# Revit family: KEUCO_14909011037_
name_source: partatom
category: Generic Models
revit_build: Autodesk Revit 2016 (Build: 20150220_1215(x64)
units: mm (PartAtom-declared; Revit-internal decimal feet)

## family parameters
Always vertical = No
Can host rebar = No
Cut with Voids When Loaded = No
Part Type = Normal
Room Calculation Point = No
Round Connector Dimension = Use Diameter
Shared = No
Work Plane-Based = Yes

## types (9) — shared parameters
Default Elevation = 1219 mm
Manufacturer = KEUCO
Serie = Plan
URL = https://www.keuco.com
zero-valued in all types: Gewicht

## per-type parameters (varying)
| type | Ausschreibungstext | Description | Material Tablett | Rahmen Material |
| 14909011037 | KEUCO PLAN Winkelgriff 135° mit Seifenablage, rechte Ausführung, 14909011037
hochglanzverchromter Winkelgriff 135° mit integrierter Seifenablage, 
in ästhetischem, funktionalem Design
rechte Ausführung,
speziell für Wannen-Bereich, als Hilfe zum Festhalten und Abstützen, 
mit integrierter Seifenablage aus Kunststoff (schlagzähes Polysterol), schwarzgrau (RAL 7021),
Ablagefläche 154 mm Breite, 23 mm Höhe, Tiefe 67 mm,
Winkelgriff bis 115 kg belastbar, antistatisch, leicht zu reinigen,
Außenmaß gesamt 444/201 mm,
Rohrdurchmesser 25 mm, 3 Befestigungspunkte, 
Gesamtbreite 444 mm, Gesamthöhe 201 mm, 
Ausladung 108 mm, Wandabstand 83 mm
Der Winkelgriff wird verdeckt angebracht

Lieferung inkl. korrosionsfreiem Befestigungsmaterial | mit Seifenablage, rechte Ausführung | Lichtgrau (RAL 7035) | Edelstahl |
| 14909011038 | KEUCO PLAN Winkelgriff 135° mit Seifenablage, rechte Ausführung, 14909011038
hochglanzverchromter Winkelgriff 135° mit integrierter Seifenablage, 
in ästhetischem, funktionalem Design
rechte Ausführung,
speziell für Wannen-Bereich, als Hilfe zum Festhalten und Abstützen, 
mit integrierter Seifenablage aus Kunststoff (schlagzähes Polysterol), lichtgrau (RAL 7035),
Ablagefläche 154 mm Breite, 23 mm Höhe, Tiefe 67 mm,
Winkelgriff bis 115 kg belastbar, antistatisch, leicht zu reinigen,
Außenmaß gesamt 444/201 mm,
Rohrdurchmesser 25 mm, 3 Befestigungspunkte, 
Gesamtbreite 444 mm, Gesamthöhe 201 mm, 
Ausladung 108 mm, Wandabstand 83 mm
Der Winkelgriff wird verdeckt angebracht

Lieferung inkl. korrosionsfreiem Befestigungsmaterial | mit Seifenablage, rechte Ausführung | Lichtgrau (RAL 7035) | verchromt |
| 14909011051 | KEUCO PLAN Winkelgriff 135° mit Seifenablage, rechte Ausführung, 14909011051
hochglanzverchromter Winkelgriff 135° mit integrierter Seifenablage, 
in ästhetischem, funktionalem Design
rechte Ausführung,
speziell für Wannen-Bereich, als Hilfe zum Festhalten und Abstützen, 
mit integrierter Seifenablage aus Kunststoff (schlagzähes Polysterol), weiß (RAL 9010),
Ablagefläche 154 mm Breite, 23 mm Höhe, Tiefe 67 mm,
Winkelgriff bis 115 kg belastbar, antistatisch, leicht zu reinigen,
Außenmaß gesamt 444/201 mm,
Rohrdurchmesser 25 mm, 3 Befestigungspunkte, 
Gesamtbreite 444 mm, Gesamthöhe 201 mm, 
Ausladung 108 mm, Wandabstand 83 mm
Der Winkelgriff wird verdeckt angebracht

Lieferung inkl. korrosionsfreiem Befestigungsmaterial | mit Seifenablage, rechte Ausführung | Weiß (RAL 9010) | verchromt |
| 14909071037 | KEUCO PLAN Winkelgriff 135° mit Seifenablage, rechte Ausführung, 14909071037
Winkelgriff 135° aus hochwertigem Edelstahl mit integrierter Seifenablage, 
in ästhetischem, funktionalem Design
rechte Ausführung,
speziell für Wannen-Bereich, als Hilfe zum Festhalten und Abstützen, 
mit integrierter Seifenablage aus Kunststoff (schlagzähes Polysterol), schwarzgrau (RAL 7021),
Ablagefläche 154 mm Breite, 23 mm Höhe, Tiefe 67 mm,
Winkelgriff bis 115 kg belastbar, antistatisch, leicht zu reinigen,
Außenmaß gesamt 444/201 mm,
Rohrdurchmesser 25 mm, 3 Befestigungspunkte, 
Gesamtbreite 444 mm, Gesamthöhe 201 mm, 
Ausladung 108 mm, Wandabstand 83 mm
Der Winkelgriff wird verdeckt angebracht

Lieferung inkl. korrosionsfreiem Befestigungsmaterial | mit Seifenablage, rechte Ausführung | schwarzgrau (RAL 7021) | Edelstahl |
| 14909071038 | KEUCO PLAN Winkelgriff 135° mit Seifenablage, rechte Ausführung, 14909071038
Winkelgriff 135° aus hochwertigem Edelstahl mit integrierter Seifenablage, 
in ästhetischem, funktionalem Design
rechte Ausführung,
speziell für Wannen-Bereich, als Hilfe zum Festhalten und Abstützen, 
mit integrierter Seifenablage aus Kunststoff (schlagzähes Polysterol), .lichtgrau (RAL 7035,
Ablagefläche 154 mm Breite, 23 mm Höhe, Tiefe 67 mm,
Winkelgriff bis 115 kg belastbar, antistatisch, leicht zu reinigen,
Außenmaß gesamt 444/201 mm,
Rohrdurchmesser 25 mm, 3 Befestigungspunkte, 
Gesamtbreite 444 mm, Gesamthöhe 201 mm, 
Ausladung 108 mm, Wandabstand 83 mm
Der Winkelgriff wird verdeckt angebracht

Lieferung inkl. korrosionsfreiem Befestigungsmaterial | mit Seifenablage, rechte Ausführung | Lichtgrau (RAL 7035) | Edelstahl |
| 14909071051 | KEUCO PLAN Winkelgriff 135° mit Seifenablage, rechte Ausführung, 14909071051
Winkelgriff 135° aus hochwertigem Edelstahl mit integrierter Seifenablage, 
in ästhetischem, funktionalem Design
rechte Ausführung,
speziell für Wannen-Bereich, als Hilfe zum Festhalten und Abstützen, 
mit integrierter Seifenablage aus Kunststoff (schlagzähes Polysterol), weiß (RAL 9010
Ablagefläche 154 mm Breite, 23 mm Höhe, Tiefe 67 mm,
Winkelgriff bis 115 kg belastbar, antistatisch, leicht zu reinigen,
Außenmaß gesamt 444/201 mm,
Rohrdurchmesser 25 mm, 3 Befestigungspunkte, 
Gesamtbreite 444 mm, Gesamthöhe 201 mm, 
Ausladung 108 mm, Wandabstand 83 mm
Der Winkelgriff wird verdeckt angebracht

Lieferung inkl. korrosionsfreiem Befestigungsmaterial | mit Seifenablage, rechte Ausführung | Weiß (RAL 9010) | Edelstahl |
| 14909171037 |  | -- | schwarzgrau (RAL 7021) | Aluminium silber-eloxiert (E6 EV1)Aluminium 1100-H18 |
| 14909171038 | KEUCO PLAN Winkelgriff 135° mit Seifenablage, rechte Ausführung, 14909171038
Winkelgriff 135° aus silber-eloxiertem Aluminium mit integrierter Seifenablage, 
in ästhetischem, funktionalem Design
rechte Ausführung,
speziell für Wannen-Bereich, als Hilfe zum Festhalten und Abstützen, 
mit integrierter Seifenablage aus Kunststoff (schlagzähes Polysterol), lichtgrau (RAL 7035),
Ablagefläche 154 mm Breite, 23 mm Höhe, Tiefe 67 mm,
Winkelgriff bis 115 kg belastbar, antistatisch, leicht zu reinigen,
Außenmaß gesamt 444/201 mm,
Rohrdurchmesser 25 mm, 3 Befestigungspunkte, 
Gesamtbreite 444 mm, Gesamthöhe 201 mm, 
Ausladung 108 mm, Wandabstand 83 mm
Der Winkelgriff wird verdeckt angebracht

Lieferung inkl. korrosionsfreiem Befestigungsmaterial | mit Seifenablage, rechte Ausführung | Lichtgrau (RAL 7035) | Aluminium silber-eloxiert (E6 EV1)Aluminium 1100-H18 |
| 14909171051 | KEUCO PLAN Winkelgriff 135° mit Seifenablage, rechte Ausführung, 14909171051
Winkelgriff 135° aus silber-eloxiertem Aluminium mit integrierter Seifenablage, 
in ästhetischem, funktionalem Design
rechte Ausführung,
speziell für Wannen-Bereich, als Hilfe zum Festhalten und Abstützen, 
mit integrierter Seifenablage aus Kunststoff (schlagzähes Polysterol), weiß (RAL 9010),
Ablagefläche 154 mm Breite, 23 mm Höhe, Tiefe 67 mm,
Winkelgriff bis 115 kg belastbar, antistatisch, leicht zu reinigen,
Außenmaß gesamt 444/201 mm,
Rohrdurchmesser 25 mm, 3 Befestigungspunkte, 
Gesamtbreite 444 mm, Gesamthöhe 201 mm, 
Ausladung 108 mm, Wandabstand 83 mm
Der Winkelgriff wird verdeckt angebracht

Lieferung inkl. korrosionsfreiem Befestigungsmaterial | mit Seifenablage, rechte Ausführung | Weiß (RAL 9010) | Aluminium silber-eloxiert (E6 EV1)Aluminium 1100-H18 |

note: column(s) folded — value = type name in every type: Artikelnummer

## geometry (parser evidence)
native form markers: Sweep x3
no freeform markers — native parametric forms only
